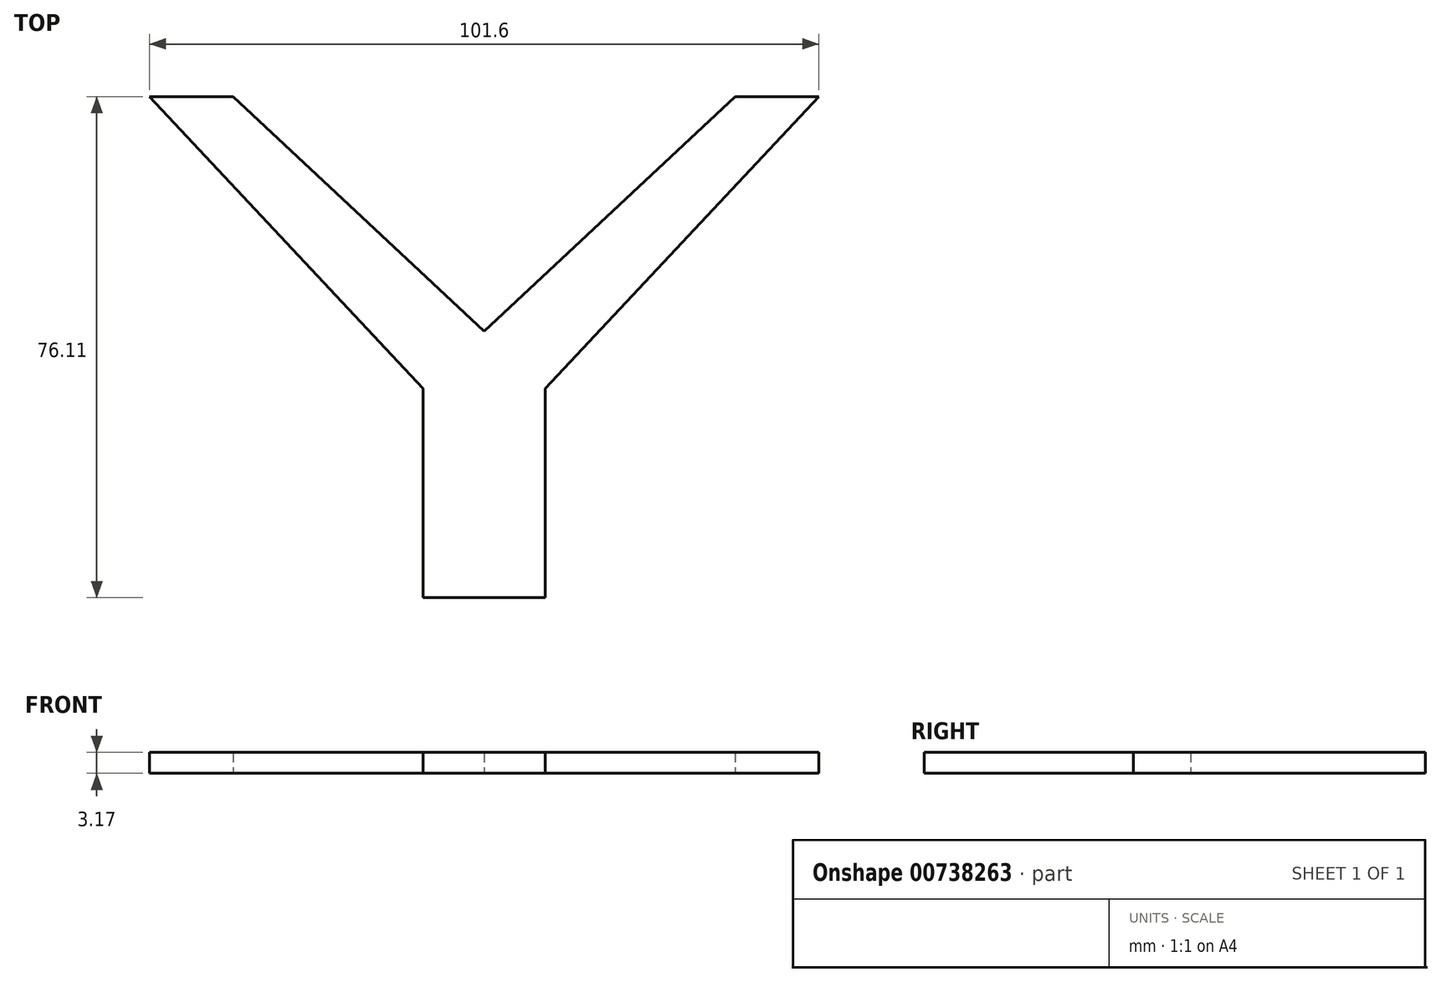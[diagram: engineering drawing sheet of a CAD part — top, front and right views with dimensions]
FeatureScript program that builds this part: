
annotation { "Feature Type Name" : "Feature", "Feature Type Description" : "" }
export const myFeature = defineFeature(function(context is Context, id is Id, definition is map)
    precondition{}
    {
        {
            var Q0;
            Q0=qCreatedBy(makeId("Top.planeOp"),FACE);
            var sketch = newSketch(context, id + "F0", { "sketchPlane" : qUnion([Q0])});
            skLineSegment(sketch, "E0", {"start": v(-9.27, 9.9) * mm, "end": v(-50.8, 54.26) * mm});
            skLineSegment(sketch, "E1", {"start": v(9.27, 9.9) * mm, "end": v(50.8, 54.26) * mm});
            skLineSegment(sketch, "E2", {"start": v(50.8, 54.26) * mm, "end": v(38.1, 54.26) * mm});
            skLineSegment(sketch, "E3", {"start": v(38.1, 54.26) * mm, "end": v(0, 18.58) * mm});
            skLineSegment(sketch, "E4", {"start": v(0, 18.58) * mm, "end": v(-38.1, 54.26) * mm});
            skLineSegment(sketch, "E5", {"start": v(-50.8, 54.26) * mm, "end": v(-38.1, 54.26) * mm});
            skPoint(sketch, "E6.visualSharp", {"position": v(0, 0) * mm});
            skLineSegment(sketch, "E7", {"start": v(-9.27, 9.9) * mm, "end": v(-9.27, -21.85) * mm});
            skLineSegment(sketch, "E8", {"start": v(-9.27, -21.85) * mm, "end": v(9.27, -21.85) * mm});
            skLineSegment(sketch, "E9", {"start": v(9.27, -21.85) * mm, "end": v(9.27, 9.9) * mm});
            skSolve(sketch);
        }
        {
            var Q0;
            Q0=makeQuery(id+"F0.imprint","IMPRINT",FACE,{"disambiguationData":[TD([[makeQuery(id+"F0.imprint","IMPRINT",EDGE,{"derivedFrom":sQuery(id+"F0.wireOp",EDGE,"E0")}),-1.0]])]});
            extrude(context, id + "F1", {"entities" : qUnion([Q0]), "depth" : 3.17 * mm, "offsetDistance" : 25.4 * mm});
        }
    });
